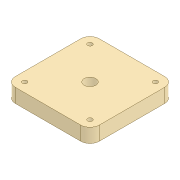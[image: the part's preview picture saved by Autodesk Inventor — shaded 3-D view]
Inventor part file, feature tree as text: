
AUTODESK INVENTOR PART (.ipt)
format: ipt  version: 2020 (Build 240168000, 168)  size: 108,544 bytes
history: native  units: mm
features: mirror x2, other x1, extrude x1, sketch x1
ambient origin geometry x8: Origin, YZ Plane, XZ Plane, XY Plane, X Axis, Y Axis, Z Axis, Center Point
bodies: Body1 (feature_tree)
feature tree (5):
  other  "Sólido1"
  extrude  "Extrusão1"  Depth=36.0mm
  mirror  "Espelhamento1"
  mirror  "Espelhamento2"
  sketch  "Esboço1"  dims[d0=10.0mm d1=36.0mm d2=36.0mm d3=8.0mm d4=4.0mm d5=12.0mm d6=0.0mm d7=8.0mm d8=8.0mm]
